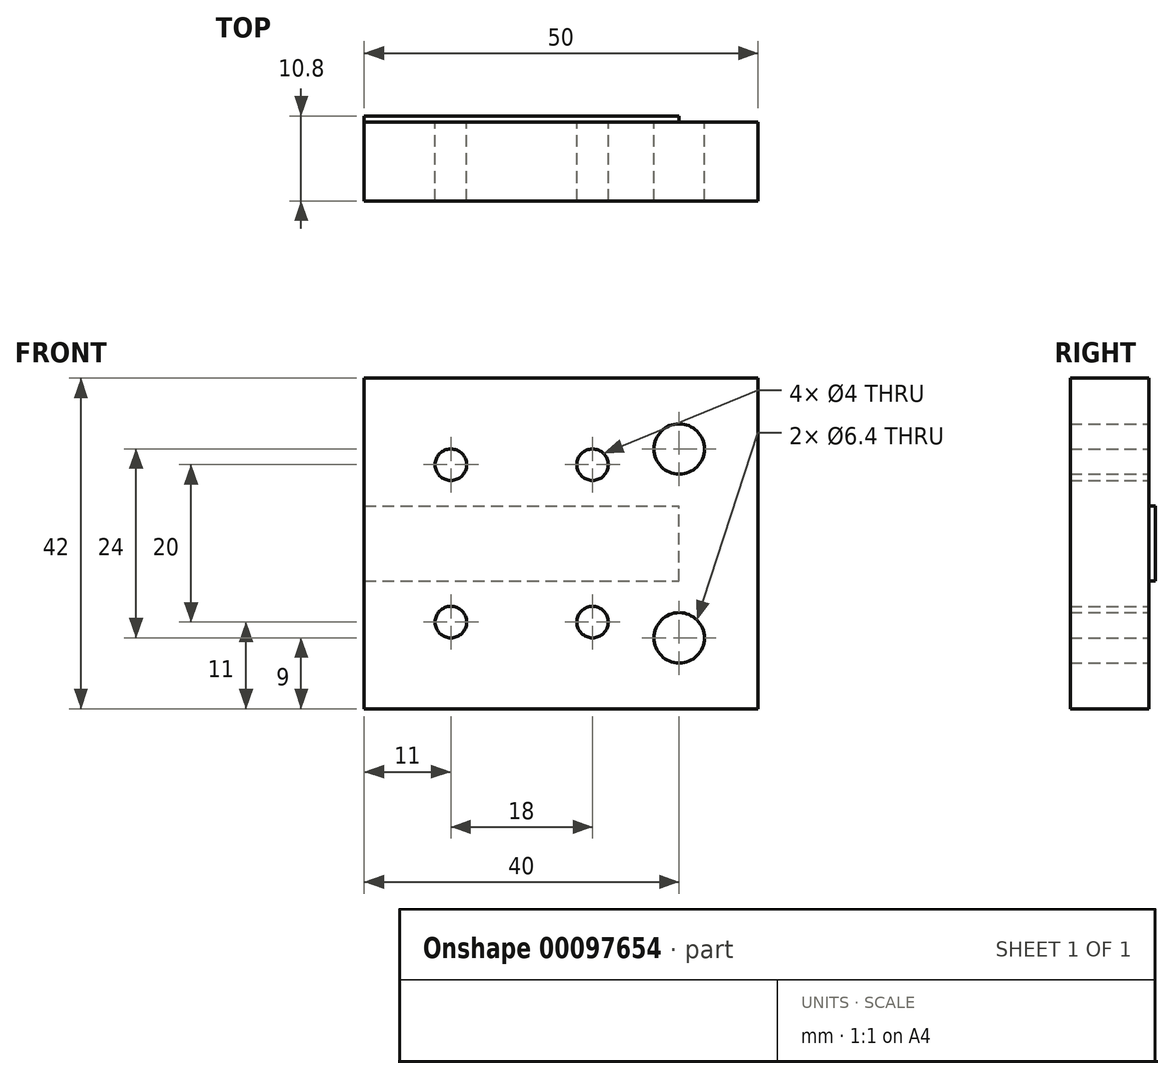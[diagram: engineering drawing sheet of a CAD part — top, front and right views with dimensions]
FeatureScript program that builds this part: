
annotation { "Feature Type Name" : "Feature", "Feature Type Description" : "" }
export const myFeature = defineFeature(function(context is Context, id is Id, definition is map)
    precondition{}
    {
        {
            var Q0;
            Q0=qCreatedBy(makeId("Front.planeOp"),FACE);
            var sketch = newSketch(context, id + "F0", { "sketchPlane" : qUnion([Q0])});
            skLineSegment(sketch, "E0.bottom", {"start": v(20, -21) * mm, "end": v(-20, -21) * mm});
            skLineSegment(sketch, "E0.top", {"start": v(20, 21) * mm, "end": v(-20, 21) * mm});
            skLineSegment(sketch, "E0.left", {"start": v(20, -21) * mm, "end": v(20, 21) * mm, "construction": true});
            skLineSegment(sketch, "E0.right", {"start": v(-20, -21) * mm, "end": v(-20, 21) * mm});
            skPoint(sketch, "E0.middle", {"position": v(0, 0) * mm});
            skLineSegment(sketch, "E1", {"start": v(20, 21) * mm, "end": v(30, 21) * mm});
            skLineSegment(sketch, "E2", {"start": v(20, -21) * mm, "end": v(30, -21) * mm});
            skLineSegment(sketch, "E3", {"start": v(30, -21) * mm, "end": v(30, 21) * mm});
            skLineSegment(sketch, "E4", {"start": v(5, 21) * mm, "end": v(5, -21) * mm, "construction": true});
            skCircle(sketch, "E5", {"center": v(20, 12) * mm, "radius": 3.2 * mm});
            skCircle(sketch, "E6", {"center": v(20, -12) * mm, "radius": 3.2 * mm});
            skPoint(sketch, "E7", {"position": v(5, 0) * mm});
            skLineSegment(sketch, "E8", {"start": v(5, 0) * mm, "end": v(20, 0) * mm, "construction": true});
            skPoint(sketch, "E8.endSnap0", {"position": v(30, 0) * mm});
            skLineSegment(sketch, "E9", {"start": v(20, 12) * mm, "end": v(20, -12) * mm, "construction": true});
            skSolve(sketch);
        }
        {
            var Q0;
            Q0=qCreatedBy(makeId("Front.planeOp"),FACE);
            var sketch = newSketch(context, id + "F1", { "sketchPlane" : qUnion([Q0])});
            skCircle(sketch, "E10", {"center": v(-9, 10) * mm, "radius": 2 * mm});
            skCircle(sketch, "E11", {"center": v(-9, -10) * mm, "radius": 2 * mm});
            skCircle(sketch, "E12", {"center": v(9, 10) * mm, "radius": 2 * mm});
            skCircle(sketch, "E13", {"center": v(9, -10) * mm, "radius": 2 * mm});
            skLineSegment(sketch, "E14", {"start": v(9, 10) * mm, "end": v(-9, -10) * mm, "construction": true});
            skPoint(sketch, "E15", {"position": v(0, 0) * mm});
            skSolve(sketch);
        }
        {
            var Q0;
            Q0 = qSketchRegion(id + "F0", true);
            extrude(context, id + "F2", {"entities" : qUnion([Q0]), "depth" : 10 * mm});
        }
        {
            var Q0;
            Q0 = qSketchRegion(id + "F1", true);
            extrude(context, id + "F3", {"entities" : qUnion([Q0]), "operationType" : NewBodyOperationType.REMOVE, "endBound" : BoundingType.UP_TO_NEXT, "depth" : 25 * mm});
        }
        {
            var Q0;
            Q0=makeQuery(id+"F2.opExtrude","CAP_FACE",FACE,{"disambiguationData":[OSD([sQuery(id+"F0.wireOp",EDGE,"E0.bottom"),sQuery(id+"F0.wireOp",EDGE,"E0.top"),sQuery(id+"F0.wireOp",EDGE,"E0.right"),sQuery(id+"F0.wireOp",EDGE,"E1"),sQuery(id+"F0.wireOp",EDGE,"E2"),sQuery(id+"F0.wireOp",EDGE,"E3"),sQuery(id+"F0.wireOp",EDGE,"E5"),sQuery(id+"F0.wireOp",EDGE,"E6")])],"isStart":true});
            var sketch = newSketch(context, id + "F4", { "sketchPlane" : qUnion([Q0])});
            skLineSegment(sketch, "E16.bottom", {"start": v(20, -4.75) * mm, "end": v(-20, -4.75) * mm});
            skLineSegment(sketch, "E16.top", {"start": v(20, 4.75) * mm, "end": v(-20, 4.75) * mm});
            skLineSegment(sketch, "E16.left", {"start": v(20, -4.75) * mm, "end": v(20, 4.75) * mm});
            skLineSegment(sketch, "E16.right", {"start": v(-20, -4.75) * mm, "end": v(-20, 4.75) * mm});
            skPoint(sketch, "E16.middle", {"position": v(0, 0) * mm});
            skSolve(sketch);
        }
        {
            var Q0;
            Q0 = qSketchRegion(id + "F4", true);
            extrude(context, id + "F5", {"entities" : qUnion([Q0]), "operationType" : NewBodyOperationType.ADD, "depth" : 0.8 * mm});
        }
    });
